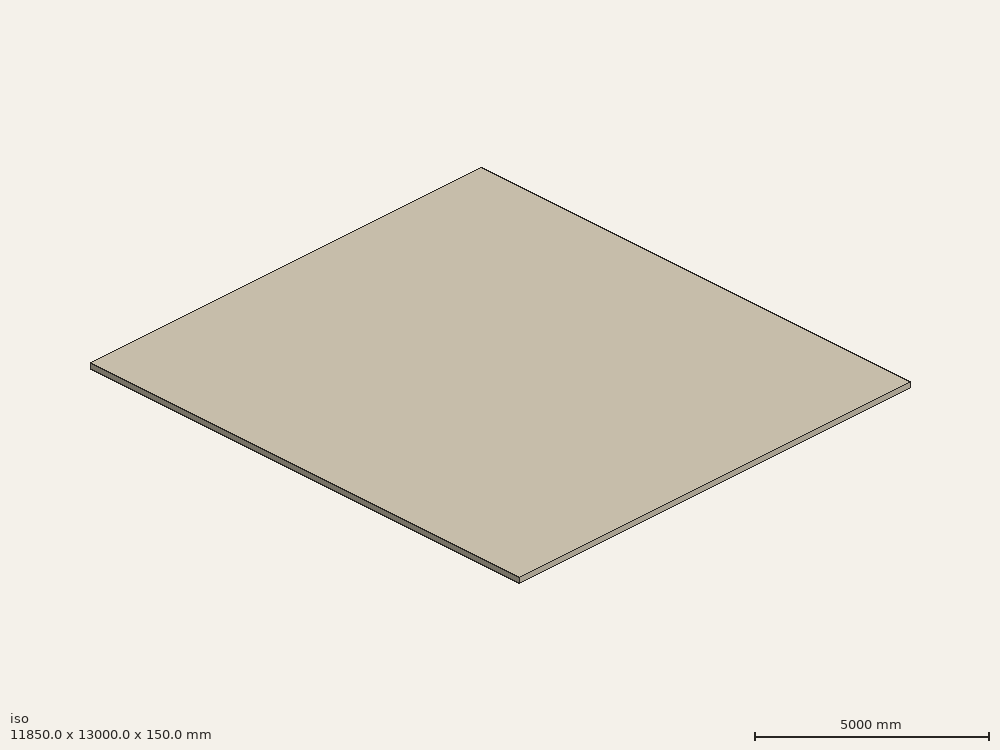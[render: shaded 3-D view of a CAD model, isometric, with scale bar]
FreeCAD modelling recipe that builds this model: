
FCSTD DOCUMENT  (FreeCAD 2024.1006R14555 (Git shallow))
Label: плита
License: All rights reserved
objects: Sketcher::SketchObject×3, Part::FeaturePython×2, PartDesign::Pad×1, PartDesign::Body×1, App::DocumentObjectGroupPython×1
note: 12 computed .brp shape members not serialized (recipe doc carries the construction recipe); baked Part::Feature solids carry a one-line shape summary decoded from their .brp

FEATURE [Sketcher::SketchObject] Sketch
  ArcFitTolerance = 1e-06
  AttachmentSupport = -> [XY_Plane]
  ExternalBSplineMaxDegree = 5
  ExternalBSplineTolerance = 0.0001
  FullyConstrained = true
  InternalTolerance = 1e-06
  InvalidShape = false
  MakeInternals = false
  MapMode = 5
  Support = -> [XY_Plane]
  TreeRank = 11
  ValidateShape = false
  sketch-geometry (4):
    g0: LineSegment StartX=11850 StartY=0 StartZ=0 EndX=0 EndY=0 EndZ=0
    g1: LineSegment StartX=0 StartY=0 StartZ=0 EndX=0 EndY=13000 EndZ=0
    g2: LineSegment StartX=0 StartY=13000 StartZ=0 EndX=11850 EndY=13000 EndZ=0
    g3: LineSegment StartX=11850 StartY=13000 StartZ=0 EndX=11850 EndY=0 EndZ=0
  constraints (11):
    c: Coincident(g0,g1)
    c: Coincident(g1,g2)
    c: Coincident(g2,g3)
    c: Coincident(g3,g0)
    c: Horizontal(g0)
    c: Horizontal(g2)
    c: Vertical(g1)
    c: Vertical(g3)
    c: DistanceX(g2,g2) = 11850
    c: DistanceY(g1,g1) = 13000
    c: Coincident(g0,g-1)
FEATURE [PartDesign::Pad] Pad
  AddSubType = 0
  AlongSketchNormal = false
  AutoTaperInnerAngle = true
  CheckUpToFaceLimits = true
  ClaimChildren = false
  Direction = (0,0,1)
  Fit = 0
  FitJoin = 0
  InnerFit = 0
  InnerFitJoin = 0
  InvalidShape = false
  Length = 150
  Length2 = 10
  Linearize = true
  NewSolid = false
  Profile = -> Sketch
  ReferenceAxis = -> Sketch [N_Axis]
  Suppress = false
  TaperInnerAngle = 0
  TaperInnerAngleRev = 0
  TreeRank = 12
  Type = 0
  ValidateShape = false
  _ProfileBasedVersion = 1
FEATURE [PartDesign::Body] Body
  AutoGroupSolids = false
  ClaimAllChildren = false
  ExportMode = 0
  Group = -> [Sketch,Pad]
  InvalidShape = false
  Origin = -> Origin
  Tip = -> Pad
  TreeRank = 10
  ValidateShape = false
  _ExportChildren = -> [Pad]
  _GroupVersion = 1
FEATURE [Sketcher::SketchObject] Sketch001
  ArcFitTolerance = 1e-06
  AttachmentSupport = -> [Pad]
  ExternalBSplineMaxDegree = 5
  ExternalBSplineTolerance = 0.0001
  FullyConstrained = false
  InternalTolerance = 1e-06
  InvalidShape = false
  MakeInternals = false
  MapMode = 5
  Placement = pos=(0,0,0) rot=(1,0,0;1.5708rad)
  Support = -> [Pad]
  TreeRank = 17
  ValidateShape = false
  sketch-geometry (1):
    g0: LineSegment StartX=50 StartY=56 StartZ=0 EndX=11800 EndY=56 EndZ=0
FEATURE [Part::FeaturePython] Rebar  label="StraightRebar"  # Arch/BIM 110 (typed FeaturePython)
  Amount = 66
  AmountCheck = false
  Base = -> Sketch001
  Cover = 50
  CoverAlong = Bottom Side
  Diameter = 12
  Direction = (0,0,0)
  Distance = 0
  FrontCover = 50
  HorizontalArea = 0
  Host = -> Pad
  IfcType = 110
  InvalidShape = false
  LeftBottomCover = 50
  Length = 11750
  Mark = StraightRebar
  MoveBase = false
  MoveWithHost = false
  OffsetEnd = 56
  OffsetStart = 56
  Orientation = Horizontal
  PerimeterLength = 0
  PlacementList = 66 placements: arithmetic series from (0,56,-1.24345e-14) step (0,198.277,-4.40263e-14) to (0,12944,-2.87415e-12)
  RebarShape = 0
  RightTopCover = 50
  Rounding = 0
  Spacing = 198.277
  TotalLength = 775500
  TreeRank = 18
  TrueSpacing = 200
  ValidateShape = false
  VerticalArea = 0
FEATURE [Sketcher::SketchObject] Sketch002
  ArcFitTolerance = 1e-06
  AttachmentSupport = -> [Pad]
  ExternalBSplineMaxDegree = 5
  ExternalBSplineTolerance = 0.0001
  FullyConstrained = false
  InternalTolerance = 1e-06
  InvalidShape = false
  MakeInternals = false
  MapMode = 5
  Placement = pos=(0,0,0) rot=(0.57735,-0.57735,-0.57735;2.0944rad)
  Support = -> [Pad]
  TreeRank = 21
  ValidateShape = false
  sketch-geometry (1):
    g0: LineSegment StartX=-12950 StartY=68 StartZ=0 EndX=-50 EndY=68 EndZ=0
FEATURE [Part::FeaturePython] Rebar001  label="StraightRebar001"  # Arch/BIM 110 (typed FeaturePython)
  Amount = 61
  AmountCheck = false
  Base = -> Sketch002
  Cover = 62
  CoverAlong = Bottom Side
  Diameter = 12
  Direction = (0,0,0)
  Distance = 0
  FrontCover = 50
  HorizontalArea = 0
  Host = -> Pad
  IfcType = 110
  InvalidShape = false
  LeftBottomCover = 50
  Length = 12900
  Mark = StraightRebar001
  MoveBase = false
  MoveWithHost = false
  OffsetEnd = 56
  OffsetStart = 56
  Orientation = Horizontal
  PerimeterLength = 0
  PlacementList = 61 placements: arithmetic series from (56,0,0) step (195.633,0,0) to (11794,0,0)
  RebarShape = 0
  RightTopCover = 50
  Rounding = 0
  Spacing = 195.633
  TotalLength = 786900
  TreeRank = 22
  TrueSpacing = 200
  ValidateShape = false
  VerticalArea = 0
FEATURE [App::DocumentObjectGroupPython] SlabReinforcement  # scripted group (container) (typed FeaturePython)
  ClaimAllChildren = true
  CrossAmountSpacingCheck = false
  CrossAmountValue = 3
  CrossBentBarAngle = 135
  CrossBentBarLength = 50
  CrossBottomCover = 50
  CrossDiameter = 12
  CrossDistributionRebarsAmount = 3
  CrossDistributionRebarsAmountSpacingCheck = true
  CrossDistributionRebarsCheck = false
  CrossDistributionRebarsDiameter = 8
  CrossDistributionRebarsSpacing = 20
  CrossFrontCover = 50
  CrossLShapeHookOrintation = 0
  CrossLeftCover = 50
  CrossRearCover = 50
  CrossRebarType = 0
  CrossRebars = -> [Rebar001]
  CrossRightCover = 50
  CrossRounding = 2
  CrossSpacingValue = 200
  CrossTopCover = 50
  ExportMode = 0
  Facename = Face1
  Group = -> [Rebar,Rebar001]
  IsMakeOrEditRequired = false
  MeshCoverAlong = 0
  ParallelAmountSpacingCheck = false
  ParallelAmountValue = 3
  ParallelBentBarAngle = 135
  ParallelBentBarLength = 50
  ParallelBottomCover = 50
  ParallelDiameter = 12
  ParallelDistributionRebarsAmount = 3
  ParallelDistributionRebarsAmountSpacingCheck = true
  ParallelDistributionRebarsCheck = false
  ParallelDistributionRebarsDiameter = 8
  ParallelDistributionRebarsSpacing = 20
  ParallelFrontCover = 50
  ParallelLShapeHookOrintation = 0
  ParallelLeftCover = 50
  ParallelRearCover = 50
  ParallelRebarType = 0
  ParallelRebars = -> [Rebar]
  ParallelRightCover = 50
  ParallelRounding = 2
  ParallelSpacingValue = 200
  ParallelTopCover = 50
  Structure = -> Pad
  TreeRank = 15
  _GroupVersion = 1
